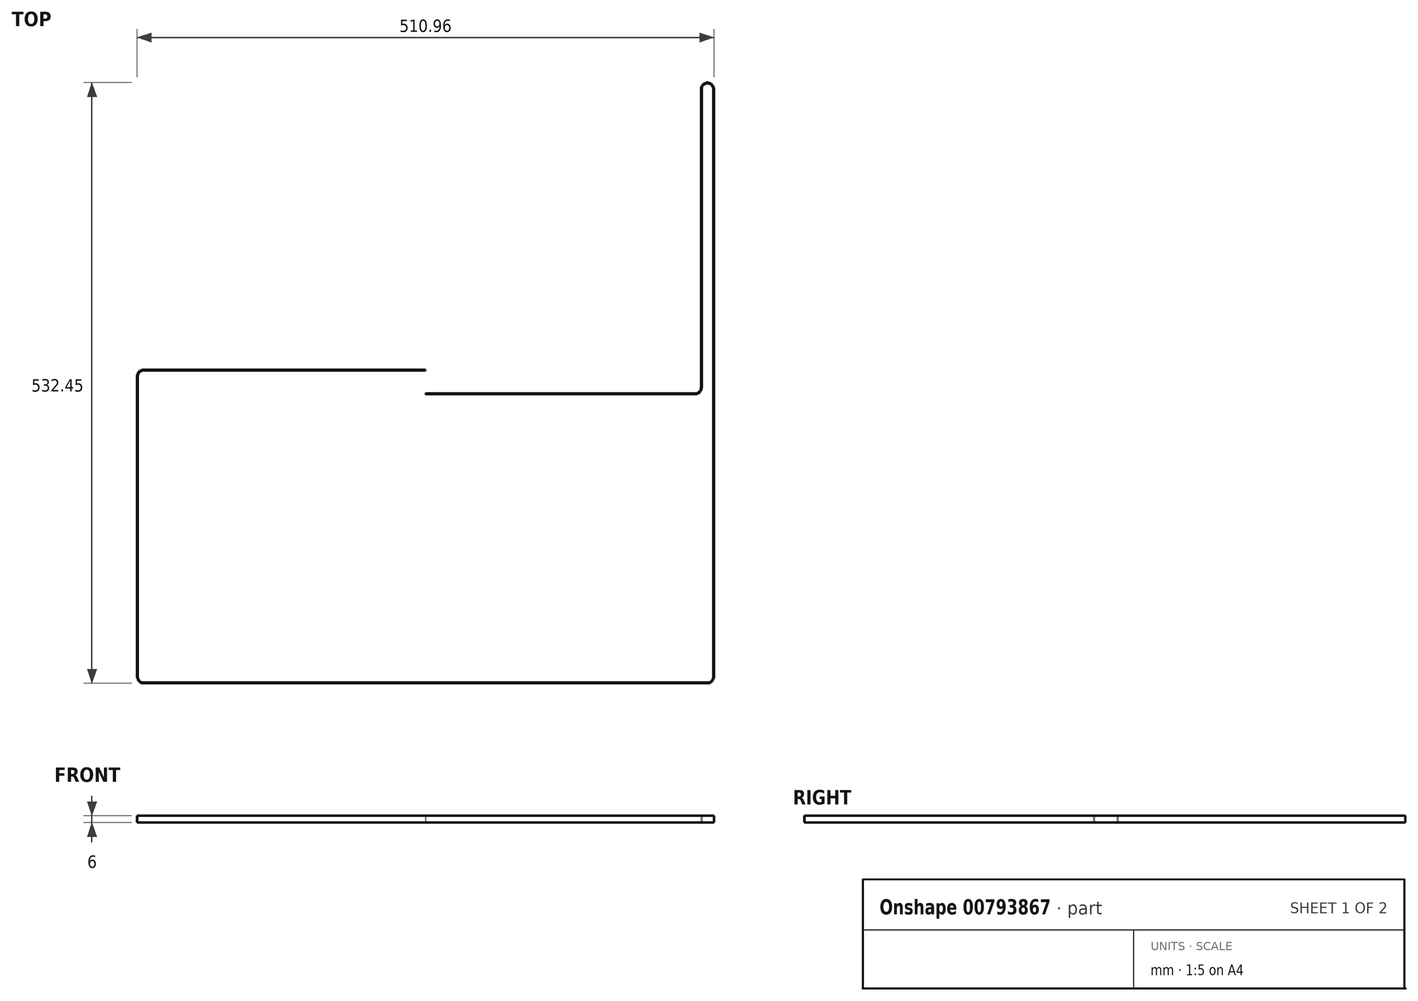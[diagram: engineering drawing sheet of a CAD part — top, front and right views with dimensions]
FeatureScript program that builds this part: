
annotation { "Feature Type Name" : "Feature", "Feature Type Description" : "" }
export const myFeature = defineFeature(function(context is Context, id is Id, definition is map)
    precondition{}
    {
        {
            var Q0;
            Q0=qCreatedBy(makeId("Top.planeOp"),FACE);
            var sketch = newSketch(context, id + "F0", { "sketchPlane" : qUnion([Q0])});
            skLineSegment(sketch, "E0", {"start": v(254.84, 259.6) * mm, "end": v(254.84, -261.4) * mm});
            skLineSegment(sketch, "E1", {"start": v(249.75, -266.5) * mm, "end": v(-249.75, -266.5) * mm});
            skArc(sketch, "E2", {"start": v(254.84, 259.6) * mm, "mid": v(249.75, 264.69) * mm, "end": v(244.65, 259.6) * mm});
            skLineSegment(sketch, "E3", {"start": v(244.65, 259.6) * mm, "end": v(244.65, -5.09) * mm});
            skArc(sketch, "E4", {"start": v(249.75, -266.5) * mm, "mid": v(253.35, -265.01) * mm, "end": v(254.84, -261.4) * mm});
            skArc(sketch, "E5", {"start": v(238.93, -10.18) * mm, "mid": v(242.53, -8.7) * mm, "end": v(244.02, -5.09) * mm});
            skLineSegment(sketch, "E6", {"start": v(238.93, -10.18) * mm, "end": v(0, -10.18) * mm});
            skArc(sketch, "E7", {"start": v(255.47, 259.6) * mm, "mid": v(249.75, 265.32) * mm, "end": v(244.02, 259.6) * mm});
            skArc(sketch, "E8", {"start": v(238.93, -10.81) * mm, "mid": v(242.98, -9.14) * mm, "end": v(244.65, -5.09) * mm});
            skArc(sketch, "E9", {"start": v(249.75, -267.13) * mm, "mid": v(253.8, -265.46) * mm, "end": v(255.47, -261.4) * mm});
            skLineSegment(sketch, "E10", {"start": v(255.47, 259.6) * mm, "end": v(255.47, -261.4) * mm});
            skLineSegment(sketch, "E11", {"start": v(-249.75, -267.13) * mm, "end": v(249.75, -267.13) * mm});
            skLineSegment(sketch, "E12", {"start": v(244.02, 259.6) * mm, "end": v(244.02, -5.09) * mm});
            skLineSegment(sketch, "E13", {"start": v(238.93, -10.81) * mm, "end": v(0, -10.81) * mm});
            skArc(sketch, "E14.MirrorCS", {"start": v(-249.75, -266.5) * mm, "mid": v(-253.35, -265.01) * mm, "end": v(-254.84, -261.4) * mm});
            skArc(sketch, "E15.MirrorCS", {"start": v(-249.75, -267.13) * mm, "mid": v(-253.8, -265.46) * mm, "end": v(-255.47, -261.4) * mm});
            skLineSegment(sketch, "E16.MirrorCS", {"start": v(-255.47, 5.09) * mm, "end": v(-255.47, -261.4) * mm});
            skLineSegment(sketch, "E17.MirrorCS", {"start": v(-254.84, 5.09) * mm, "end": v(-254.84, -261.4) * mm});
            skArc(sketch, "E18", {"start": v(-249.75, 10.18) * mm, "mid": v(-253.35, 8.7) * mm, "end": v(-254.84, 5.09) * mm});
            skLineSegment(sketch, "E19", {"start": v(0, 10.18) * mm, "end": v(-249.75, 10.18) * mm});
            skPoint(sketch, "E20.orphan", {"position": v(0, -10.19) * mm});
            skPoint(sketch, "E21.MirrorCS.end.orphan", {"position": v(0, -10.81) * mm});
            skLineSegment(sketch, "E22", {"start": v(0, -10.81) * mm, "end": v(0, -10.19) * mm});
            skLineSegment(sketch, "E23", {"start": v(-249.75, 10.81) * mm, "end": v(0, 10.81) * mm});
            skArc(sketch, "E24", {"start": v(-249.75, 10.81) * mm, "mid": v(-253.8, 9.14) * mm, "end": v(-255.47, 5.09) * mm});
            skPoint(sketch, "E25", {"position": v(0, -10.5) * mm});
            skLineSegment(sketch, "E26", {"start": v(0, 10.19) * mm, "end": v(0, 10.81) * mm});
            skPoint(sketch, "E27", {"position": v(0, 10.5) * mm});
            skLineSegment(sketch, "E28", {"start": v(-254.84, 5.09) * mm, "end": v(-255.47, 5.09) * mm});
            skPoint(sketch, "E29", {"position": v(-255.16, 5.09) * mm});
            skSolve(sketch);
        }
        {
            var Q0;
            Q0=qSketchRegion(id+"F0",true);
            extrude(context, id + "F1", {"entities" : qUnion([Q0]), "depth" : 6 * mm, "offsetDistance" : 25 * mm});
        }
    });
